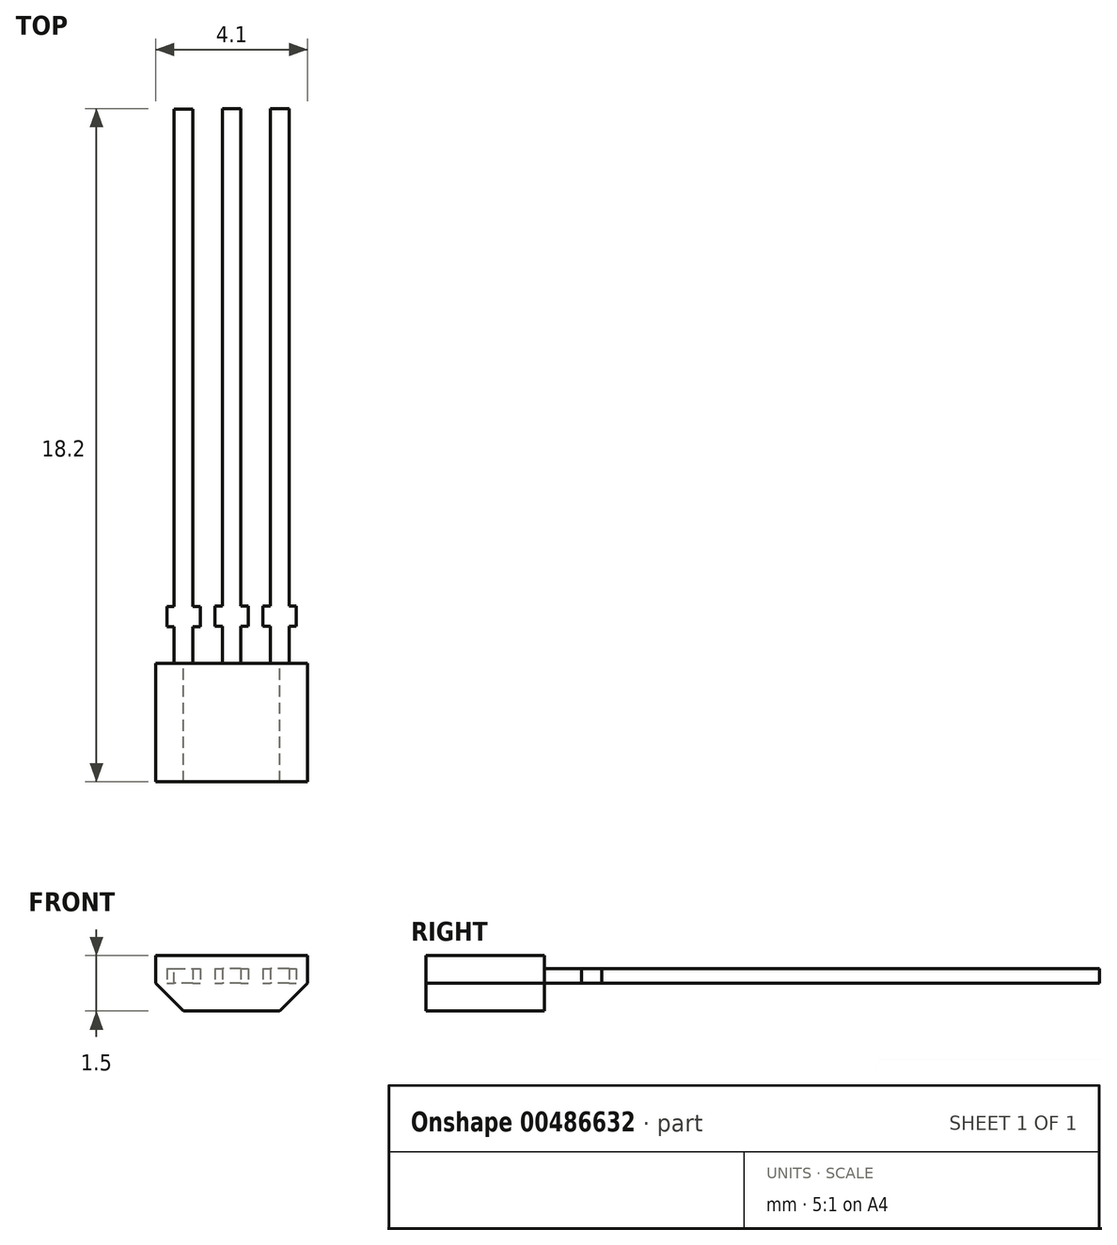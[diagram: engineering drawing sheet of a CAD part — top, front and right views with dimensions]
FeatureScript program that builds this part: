
annotation { "Feature Type Name" : "Feature", "Feature Type Description" : "" }
export const myFeature = defineFeature(function(context is Context, id is Id, definition is map)
    precondition{}
    {
        {
            var Q0;
            Q0=qCreatedBy(makeId("Front.planeOp"),FACE);
            var sketch = newSketch(context, id + "F0", { "sketchPlane" : qUnion([Q0])});
            skLineSegment(sketch, "E0", {"start": v(0, 29.64) * mm, "end": v(0, -26.7) * mm, "construction": true});
            skLineSegment(sketch, "E1.0", {"start": v(-2.05, 0.75) * mm, "end": v(2.05, 0.75) * mm});
            skLineSegment(sketch, "E2.0", {"start": v(2.05, 0.75) * mm, "end": v(2.05, 0) * mm});
            skLineSegment(sketch, "E3.0", {"start": v(-2.05, 0.75) * mm, "end": v(-2.05, 0) * mm});
            skPoint(sketch, "E4.orphan", {"position": v(-2.05, -0.27) * mm});
            skPoint(sketch, "E5.orphan", {"position": v(2.05, 0) * mm});
            skLineSegment(sketch, "E6", {"start": v(2.56, 0) * mm, "end": v(-3.05, 0) * mm, "construction": true});
            skLineSegment(sketch, "E7", {"start": v(2.05, 0) * mm, "end": v(1.3, -0.75) * mm});
            skLineSegment(sketch, "E8", {"start": v(1.3, -0.75) * mm, "end": v(-1.3, -0.75) * mm});
            skLineSegment(sketch, "E9", {"start": v(-1.3, -0.75) * mm, "end": v(-2.05, 0) * mm});
            skSolve(sketch);
        }
        {
            var Q0;
            Q0=makeQuery(id+"F0.imprint","IMPRINT",FACE,{"disambiguationData":[TD([[makeQuery(id+"F0.imprint","IMPRINT",EDGE,{"derivedFrom":sQuery(id+"F0.wireOp",EDGE,"E1.0")}),-1.0]])]});
            extrude(context, id + "F1", {"entities" : qUnion([Q0]), "depth" : 3.2 * mm});
        }
        {
            var Q0;
            Q0=qCreatedBy(makeId("Top.planeOp"),FACE);
            var sketch = newSketch(context, id + "F2", { "sketchPlane" : qUnion([Q0])});
            skLineSegment(sketch, "E10", {"start": v(0, 0) * mm, "end": v(0, 7.3) * mm, "construction": true});
            skLineSegment(sketch, "E11", {"start": v(0.25, 0) * mm, "end": v(0.25, 1) * mm});
            skLineSegment(sketch, "E12", {"start": v(0.25, 1) * mm, "end": v(0.45, 1) * mm});
            skLineSegment(sketch, "E13", {"start": v(0.45, 1) * mm, "end": v(0.45, 1.55) * mm});
            skLineSegment(sketch, "E14", {"start": v(0.45, 1.55) * mm, "end": v(0.25, 1.55) * mm});
            skLineSegment(sketch, "E15", {"start": v(0.25, 1.55) * mm, "end": v(0.25, 15) * mm});
            skLineSegment(sketch, "E16.MirrorCS", {"start": v(-0.25, 1.55) * mm, "end": v(-0.25, 15) * mm});
            skLineSegment(sketch, "E17.MirrorCS", {"start": v(-0.45, 1.55) * mm, "end": v(-0.25, 1.55) * mm});
            skLineSegment(sketch, "E18.MirrorCS", {"start": v(-0.45, 1) * mm, "end": v(-0.45, 1.55) * mm});
            skLineSegment(sketch, "E19.MirrorCS", {"start": v(-0.25, 1) * mm, "end": v(-0.45, 1) * mm});
            skLineSegment(sketch, "E20.MirrorCS", {"start": v(-0.25, 0) * mm, "end": v(-0.25, 1) * mm});
            skLineSegment(sketch, "E21", {"start": v(-0.25, 15) * mm, "end": v(0.25, 15) * mm});
            skLineSegment(sketch, "E22", {"start": v(0.25, 0) * mm, "end": v(-0.25, 0) * mm});
            skLineSegment(sketch, "E23.1.0.0", {"start": v(1.55, 0) * mm, "end": v(1.55, 1) * mm});
            skLineSegment(sketch, "E23.1.0.1", {"start": v(0.85, 1) * mm, "end": v(0.85, 1.55) * mm});
            skLineSegment(sketch, "E23.1.0.2", {"start": v(1.75, 1) * mm, "end": v(1.75, 1.55) * mm});
            skLineSegment(sketch, "E23.1.0.3", {"start": v(1.05, 0) * mm, "end": v(1.05, 1) * mm});
            skLineSegment(sketch, "E23.1.0.4", {"start": v(1.55, 0) * mm, "end": v(1.05, 0) * mm});
            skLineSegment(sketch, "E23.1.0.5", {"start": v(1.55, 1) * mm, "end": v(1.75, 1) * mm});
            skLineSegment(sketch, "E23.1.0.6", {"start": v(1.75, 1.55) * mm, "end": v(1.55, 1.55) * mm});
            skLineSegment(sketch, "E23.1.0.7", {"start": v(0.85, 1.55) * mm, "end": v(1.05, 1.55) * mm});
            skLineSegment(sketch, "E23.1.0.8", {"start": v(1.05, 1) * mm, "end": v(0.85, 1) * mm});
            skLineSegment(sketch, "E23.1.0.9", {"start": v(1.55, 1.55) * mm, "end": v(1.55, 15) * mm});
            skLineSegment(sketch, "E23.1.0.10", {"start": v(1.05, 1.55) * mm, "end": v(1.05, 15) * mm});
            skLineSegment(sketch, "E23.1.0.11", {"start": v(1.05, 15) * mm, "end": v(1.55, 15) * mm});
            skLineSegment(sketch, "E23.direction1", {"start": v(-0.25, 0) * mm, "end": v(1.05, 0) * mm, "construction": true});
            skLineSegment(sketch, "E24.1.0.0", {"start": v(-1.55, 0) * mm, "end": v(-1.55, 1) * mm});
            skLineSegment(sketch, "E24.1.0.1", {"start": v(-1.55, 15) * mm, "end": v(-1.05, 15) * mm});
            skLineSegment(sketch, "E24.1.0.2", {"start": v(-1.75, 1) * mm, "end": v(-1.75, 1.54) * mm});
            skLineSegment(sketch, "E24.1.0.3", {"start": v(-1.55, 1.54) * mm, "end": v(-1.55, 15) * mm});
            skLineSegment(sketch, "E24.1.0.4", {"start": v(-1.05, 1.54) * mm, "end": v(-1.05, 15) * mm});
            skLineSegment(sketch, "E24.1.0.5", {"start": v(-1.3, 0) * mm, "end": v(-1.3, 7.3) * mm, "construction": true});
            skLineSegment(sketch, "E24.1.0.6", {"start": v(-1.05, 0) * mm, "end": v(-1.05, 1) * mm});
            skLineSegment(sketch, "E24.1.0.7", {"start": v(-0.85, 1) * mm, "end": v(-0.85, 1.54) * mm});
            skLineSegment(sketch, "E24.1.0.8", {"start": v(-1.05, 0) * mm, "end": v(-1.55, 0) * mm});
            skLineSegment(sketch, "E24.1.0.9", {"start": v(-1.55, 1) * mm, "end": v(-1.75, 1) * mm});
            skLineSegment(sketch, "E24.1.0.10", {"start": v(-1.75, 1.54) * mm, "end": v(-1.55, 1.54) * mm});
            skLineSegment(sketch, "E24.1.0.11", {"start": v(-0.85, 1.54) * mm, "end": v(-1.05, 1.54) * mm});
            skLineSegment(sketch, "E24.1.0.12", {"start": v(-1.05, 1) * mm, "end": v(-0.85, 1) * mm});
            skLineSegment(sketch, "E24.direction1", {"start": v(-0.25, 0) * mm, "end": v(-1.55, 0) * mm, "construction": true});
            skSolve(sketch);
        }
        {
            var Q0;
            Q0=makeQuery(id+"F2.imprint","IMPRINT",FACE,{"disambiguationData":[TD([[makeQuery(id+"F2.imprint","IMPRINT",EDGE,{"derivedFrom":sQuery(id+"F2.wireOp",EDGE,"E11")}),1.0]])]});
            var Q1;
            Q1=makeQuery(id+"F2.imprint","IMPRINT",FACE,{"disambiguationData":[TD([[makeQuery(id+"F2.imprint","IMPRINT",EDGE,{"derivedFrom":sQuery(id+"F2.wireOp",EDGE,"E23.1.0.0")}),1.0]])]});
            var Q2;
            Q2=makeQuery(id+"F2.imprint","IMPRINT",FACE,{"disambiguationData":[TD([[makeQuery(id+"F2.imprint","IMPRINT",EDGE,{"derivedFrom":sQuery(id+"F2.wireOp",EDGE,"E24.1.0.0")}),-1.0]])]});
            extrude(context, id + "F3", {"entities" : qUnion([Q0, Q1, Q2]), "operationType" : NewBodyOperationType.ADD, "depth" : .4 * mm});
        }
    });
